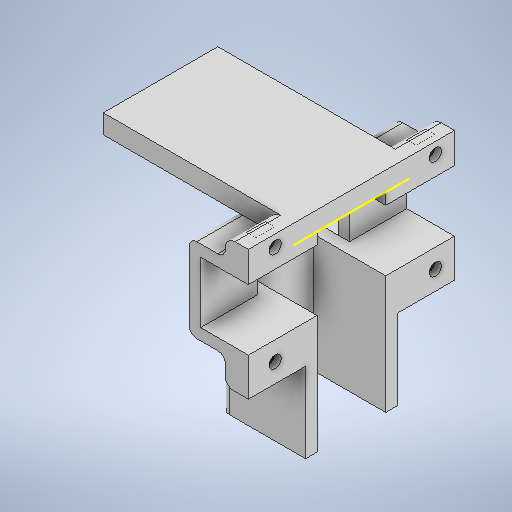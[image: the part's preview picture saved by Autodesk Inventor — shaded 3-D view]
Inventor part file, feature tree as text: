
AUTODESK INVENTOR PART (.ipt)
format: ipt  version: 2025.1 (Build 291241020, 241B)  size: 492,032 bytes
history: native  units: in
note: dims shown in document units (in); Inventor stores cm internally (conversion verified against a paired STEP export)
features: other x5, extrude x4, sketch x4, fillet x1
ambient origin geometry x8: Origin, YZ Plane, XZ Plane, XY Plane, X Axis, Y Axis, Z Axis, Center Point
bodies: Solid1 (feature_tree)
feature tree (14):
  other  "Model1Assembly.iam"
  other  "nanoMount.ipt:1"
  other  "motorMount.ipt:1"
  other  "motorMount.ipt:2"
  other  "batteryMount.ipt:1"
  extrude  "Extrusion1"  Depth=0.0787in
  extrude  "Extrusion2"  Depth=0.3937in TaperAngle=0.0deg
  extrude  "Extrusion3"  Depth=0.3937in TaperAngle=0.0deg
  extrude  "Extrusion4"  Depth=0.3937in TaperAngle=0.0deg
  fillet  "Fillet1"  Radius=0.0787in
  sketch  "Sketch4"  dims[d0=0.3937in d1=0.0787in]
  sketch  "Sketch5"  dims[d2=0.3937in d3=0.0in d4=0.3937in d5=0.0in]
  sketch  "Sketch6"  dims[d6=0.6299in d7=0.3937in d8=0.0in]
  sketch  "Sketch8"  dims[d9=0.315in d10=0.3937in d11=0.0in d12=0.0787in d13=0.0in d14=0.0in d15=0.0in]
